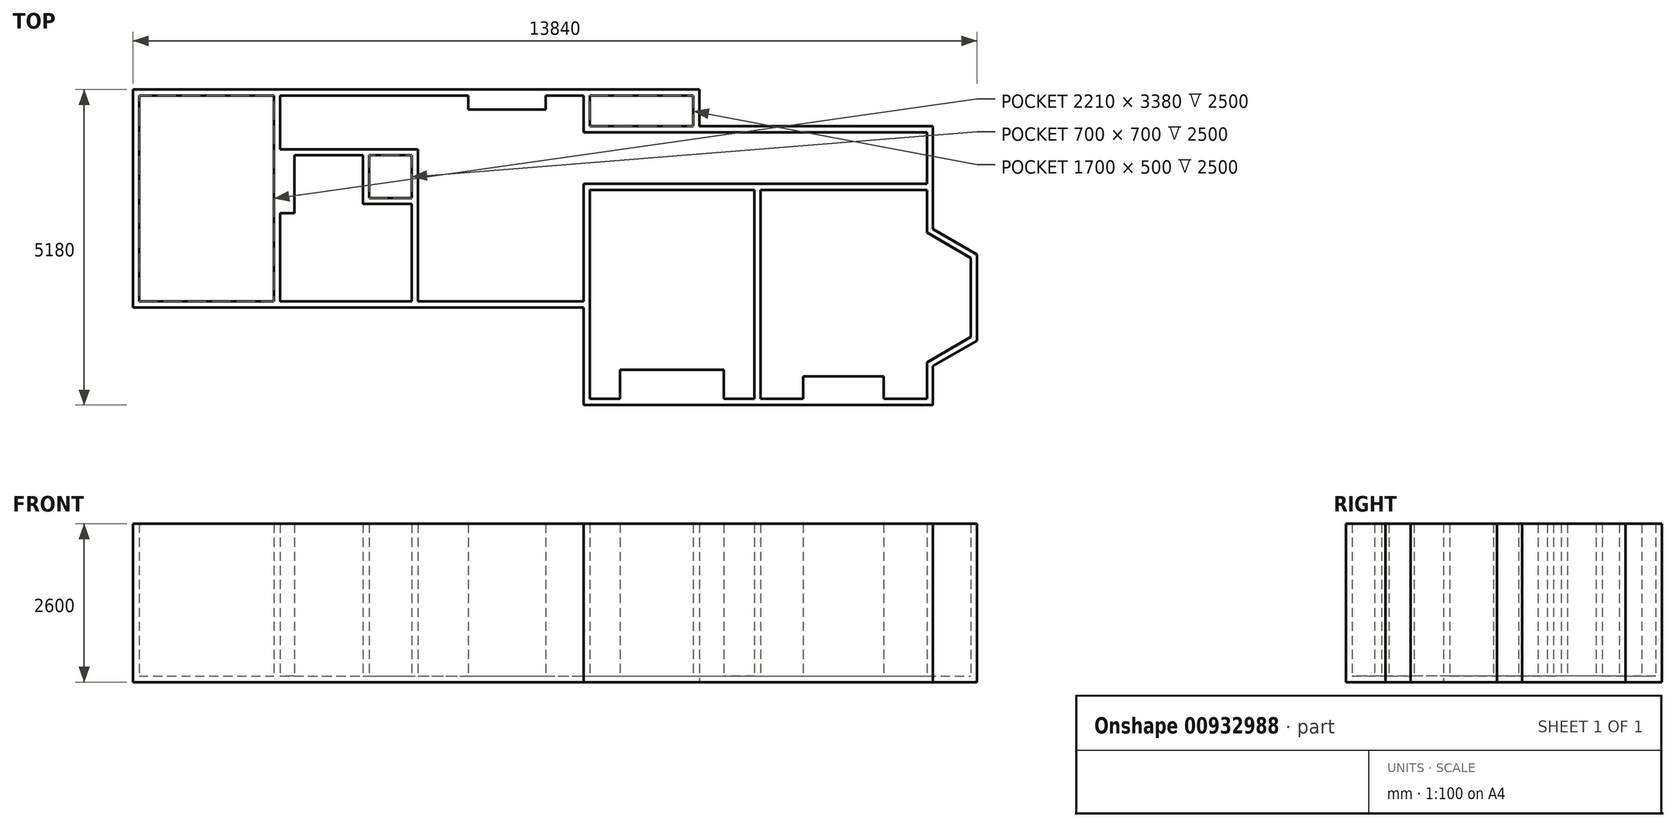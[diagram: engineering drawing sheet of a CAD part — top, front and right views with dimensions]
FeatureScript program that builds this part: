
annotation { "Feature Type Name" : "Feature", "Feature Type Description" : "" }
export const myFeature = defineFeature(function(context is Context, id is Id, definition is map)
    precondition{}
    {
        {
            var Q0;
            Q0=qCreatedBy(makeId("Top.planeOp"),FACE);
            var sketch = newSketch(context, id + "F0", { "sketchPlane" : qUnion([Q0])});
            skLineSegment(sketch, "E0", {"start": v(0, 0) * mm, "end": v(2210, 0) * mm});
            skLineSegment(sketch, "E1", {"start": v(0, 0) * mm, "end": v(0, -3380) * mm});
            skLineSegment(sketch, "E2", {"start": v(0, -3380) * mm, "end": v(2210, -3380) * mm});
            skLineSegment(sketch, "E3", {"start": v(7290, -600) * mm, "end": v(7290, 0) * mm});
            skLineSegment(sketch, "E4.0", {"start": v(-100, 100) * mm, "end": v(7390, 100) * mm});
            skLineSegment(sketch, "E4.1", {"start": v(-100, 100) * mm, "end": v(-100, -3480) * mm});
            skLineSegment(sketch, "E4.2", {"start": v(-100, -3480) * mm, "end": v(7290, -3480) * mm});
            skLineSegment(sketch, "E4.3", {"start": v(7390, -500) * mm, "end": v(7390, 0) * mm});
            skLineSegment(sketch, "E5", {"start": v(7290, 0) * mm, "end": v(7290, -600) * mm, "construction": true});
            skLineSegment(sketch, "E6", {"start": v(7390, -600) * mm, "end": v(11290, -600) * mm, "construction": true});
            skLineSegment(sketch, "E7", {"start": v(2210, -3380) * mm, "end": v(2210, 0) * mm});
            skLineSegment(sketch, "E8", {"start": v(2310, -3380) * mm, "end": v(2310, -1930) * mm});
            skLineSegment(sketch, "E9.trimOffspring", {"start": v(2310, 0) * mm, "end": v(5400, 0) * mm});
            skLineSegment(sketch, "E10.trimOffspring", {"start": v(2310, -3380) * mm, "end": v(4470, -3380) * mm});
            skLineSegment(sketch, "E11", {"start": v(2550, -980) * mm, "end": v(3670, -980) * mm});
            skLineSegment(sketch, "E12", {"start": v(4470, -1780) * mm, "end": v(4470, -3380) * mm});
            skLineSegment(sketch, "E13.0", {"start": v(4570, -880) * mm, "end": v(4570, -3380) * mm});
            skLineSegment(sketch, "E13.1", {"start": v(2310, -880) * mm, "end": v(4570, -880) * mm});
            skLineSegment(sketch, "E14.trimOffspring", {"start": v(2310, -880) * mm, "end": v(2310, 0) * mm});
            skLineSegment(sketch, "E15.trimOffspring", {"start": v(4570, -3380) * mm, "end": v(7290, -3380) * mm});
            skLineSegment(sketch, "E16", {"start": v(4570, 0) * mm, "end": v(5400, 0) * mm, "construction": true});
            skLineSegment(sketch, "E17", {"start": v(7290, 0) * mm, "end": v(6670, 0) * mm, "construction": true});
            skLineSegment(sketch, "E18", {"start": v(5400, 0) * mm, "end": v(5400, -230) * mm});
            skLineSegment(sketch, "E19", {"start": v(6670, -230) * mm, "end": v(6670, 0) * mm});
            skLineSegment(sketch, "E20", {"start": v(5400, -230) * mm, "end": v(6670, -230) * mm});
            skLineSegment(sketch, "E21.trimOffspring", {"start": v(6670, 0) * mm, "end": v(7290, 0) * mm});
            skLineSegment(sketch, "E22", {"start": v(3670, -980) * mm, "end": v(3670, -1780) * mm, "construction": true});
            skLineSegment(sketch, "E23", {"start": v(3670, -1780) * mm, "end": v(4470, -1780) * mm, "construction": true});
            skLineSegment(sketch, "E24.top", {"start": v(3670, -1780) * mm, "end": v(4470, -1780) * mm});
            skLineSegment(sketch, "E24.left", {"start": v(3670, -980) * mm, "end": v(3670, -1780) * mm});
            skLineSegment(sketch, "E25", {"start": v(2310, -3380) * mm, "end": v(2310, -1930) * mm, "construction": true});
            skLineSegment(sketch, "E26", {"start": v(3670, -980) * mm, "end": v(2550, -980) * mm});
            skLineSegment(sketch, "E27", {"start": v(2550, -980) * mm, "end": v(2550, -1930) * mm});
            skLineSegment(sketch, "E28", {"start": v(2550, -1930) * mm, "end": v(2310, -1930) * mm});
            skLineSegment(sketch, "E29", {"start": v(7390, -3480) * mm, "end": v(7390, -1550) * mm});
            skLineSegment(sketch, "E30", {"start": v(7390, -1450) * mm, "end": v(12620, -1450) * mm});
            skLineSegment(sketch, "E31", {"start": v(7390, -600) * mm, "end": v(12620, -600) * mm});
            skLineSegment(sketch, "E32.0", {"start": v(7390, -1550) * mm, "end": v(10090, -1550) * mm});
            skLineSegment(sketch, "E32.2", {"start": v(7390, -500) * mm, "end": v(9090, -500) * mm});
            skLineSegment(sketch, "E33", {"start": v(7390, -1550) * mm, "end": v(7390, -4980) * mm, "construction": true});
            skLineSegment(sketch, "E34.left", {"start": v(7390, -1550) * mm, "end": v(7390, -4980) * mm});
            skLineSegment(sketch, "E34.right", {"start": v(10090, -1550) * mm, "end": v(10090, -4980) * mm});
            skLineSegment(sketch, "E35.0", {"start": v(7290, -1550) * mm, "end": v(7290, -3380) * mm});
            skLineSegment(sketch, "E35.1", {"start": v(7290, -5080) * mm, "end": v(10190, -5080) * mm});
            skLineSegment(sketch, "E35.2", {"start": v(10190, -1550) * mm, "end": v(10190, -4980) * mm});
            skLineSegment(sketch, "E36.trimOffspring", {"start": v(7290, -3480) * mm, "end": v(7290, -5080) * mm});
            skLineSegment(sketch, "E37.trimOffspring", {"start": v(10190, -1550) * mm, "end": v(12720, -1550) * mm});
            skLineSegment(sketch, "E38", {"start": v(7390, -1450) * mm, "end": v(7290, -1450) * mm});
            skLineSegment(sketch, "E39", {"start": v(7290, -1450) * mm, "end": v(7290, -1550) * mm});
            skLineSegment(sketch, "E40", {"start": v(10190, -1550) * mm, "end": v(12920, -1550) * mm, "construction": true});
            skPoint(sketch, "E40.endSnap0", {"position": v(11455, -1550) * mm});
            skLineSegment(sketch, "E41.bottom", {"start": v(10190, -1550) * mm, "end": v(12920, -1550) * mm});
            skLineSegment(sketch, "E41.right", {"start": v(13640, -2665.7) * mm, "end": v(13640, -3964.3) * mm});
            skLineSegment(sketch, "E42.0", {"start": v(10190, -1450) * mm, "end": v(12920, -1450) * mm});
            skLineSegment(sketch, "E42.2", {"start": v(10190, -5080) * mm, "end": v(13020, -5080) * mm});
            skLineSegment(sketch, "E43", {"start": v(12920, -4980) * mm, "end": v(12920, -4380) * mm, "construction": true});
            skLineSegment(sketch, "E44", {"start": v(12920, -1550) * mm, "end": v(12920, -2250) * mm, "construction": true});
            skLineSegment(sketch, "E45", {"start": v(12920, -4980) * mm, "end": v(12920, -4380) * mm});
            skLineSegment(sketch, "E46", {"start": v(12920, -2250) * mm, "end": v(12920, -1550) * mm});
            skLineSegment(sketch, "E47", {"start": v(12920, -4980) * mm, "end": v(12210, -4980) * mm, "construction": true});
            skLineSegment(sketch, "E48.top", {"start": v(10890, -4610) * mm, "end": v(12210, -4610) * mm});
            skLineSegment(sketch, "E48.left", {"start": v(10890, -4980) * mm, "end": v(10890, -4610) * mm});
            skLineSegment(sketch, "E48.right", {"start": v(12210, -4980) * mm, "end": v(12210, -4610) * mm});
            skLineSegment(sketch, "E49.trimOffspring", {"start": v(12210, -4980) * mm, "end": v(12920, -4980) * mm});
            skLineSegment(sketch, "E50", {"start": v(12920, -2250) * mm, "end": v(13640, -2665.7) * mm});
            skLineSegment(sketch, "E51", {"start": v(12920, -4380) * mm, "end": v(13640, -3964.3) * mm});
            skPoint(sketch, "E52.start.orphan", {"position": v(13640, -4380) * mm});
            skPoint(sketch, "E53.orphan", {"position": v(13640, -1550) * mm});
            skLineSegment(sketch, "E54.0", {"start": v(13020, -2192.26) * mm, "end": v(13020, -1550) * mm});
            skLineSegment(sketch, "E54.1", {"start": v(13020, -4980) * mm, "end": v(13020, -4437.74) * mm});
            skLineSegment(sketch, "E54.2", {"start": v(13020, -4437.74) * mm, "end": v(13740, -4022.04) * mm});
            skLineSegment(sketch, "E54.3", {"start": v(13740, -2607.96) * mm, "end": v(13740, -4022.04) * mm});
            skLineSegment(sketch, "E54.4", {"start": v(13020, -2192.26) * mm, "end": v(13740, -2607.96) * mm});
            skLineSegment(sketch, "E55", {"start": v(12720, -500) * mm, "end": v(13020, -500) * mm});
            skLineSegment(sketch, "E56", {"start": v(13020, -500) * mm, "end": v(13020, -1550) * mm});
            skLineSegment(sketch, "E57", {"start": v(12620, -600) * mm, "end": v(12920, -600) * mm});
            skLineSegment(sketch, "E58", {"start": v(12920, -600) * mm, "end": v(12920, -1450) * mm});
            skLineSegment(sketch, "E59", {"start": v(13020, -4980) * mm, "end": v(13020, -5080) * mm});
            skLineSegment(sketch, "E60.trimOffspring", {"start": v(12210, -4980) * mm, "end": v(12920, -4980) * mm, "construction": true});
            skLineSegment(sketch, "E61", {"start": v(7290, -600) * mm, "end": v(7390, -600) * mm});
            skLineSegment(sketch, "E62", {"start": v(10190, -4980) * mm, "end": v(10890, -4980) * mm});
            skLineSegment(sketch, "E63.bottom", {"start": v(3770, -980) * mm, "end": v(4470, -980) * mm});
            skLineSegment(sketch, "E63.top", {"start": v(3770, -1680) * mm, "end": v(4470, -1680) * mm});
            skLineSegment(sketch, "E63.left", {"start": v(3770, -980) * mm, "end": v(3770, -1680) * mm});
            skLineSegment(sketch, "E63.right", {"start": v(4470, -980) * mm, "end": v(4470, -1680) * mm});
            skLineSegment(sketch, "E64", {"start": v(7390, -4980) * mm, "end": v(7890, -4980) * mm});
            skLineSegment(sketch, "E65", {"start": v(10090, -4980) * mm, "end": v(9590, -4980) * mm});
            skLineSegment(sketch, "E66", {"start": v(7890, -4500) * mm, "end": v(9590, -4500) * mm});
            skLineSegment(sketch, "E67", {"start": v(9590, -4500) * mm, "end": v(9590, -4980) * mm});
            skLineSegment(sketch, "E68", {"start": v(7890, -4500) * mm, "end": v(7890, -4980) * mm});
            skPoint(sketch, "E69.start.orphan", {"position": v(7890, -1550) * mm});
            skLineSegment(sketch, "E70.top", {"start": v(7390, 0) * mm, "end": v(9090, 0) * mm});
            skLineSegment(sketch, "E70.right", {"start": v(9090, -500) * mm, "end": v(9090, 0) * mm});
            skLineSegment(sketch, "E71", {"start": v(7390, 100) * mm, "end": v(9190, 100) * mm});
            skLineSegment(sketch, "E72", {"start": v(9190, 100) * mm, "end": v(9190, -500) * mm});
            skLineSegment(sketch, "E73.trimOffspring", {"start": v(9190, -500) * mm, "end": v(12720, -500) * mm});
            skSolve(sketch);
        }
        {
            var Q0;
            Q0 = qSketchRegion(id + "F0", true);
            extrude(context, id + "F1", {"entities" : qUnion([Q0]), "depth" : 2500 * mm, "offsetDistance" : 25 * mm});
        }
        {
            var Q0;
            Q0=makeQuery(id+"F1.opExtrude","CAP_FACE",FACE,{"disambiguationData":[OSD([sQuery(id+"F0.wireOp",EDGE,"E0"),sQuery(id+"F0.wireOp",EDGE,"E1"),sQuery(id+"F0.wireOp",EDGE,"E2"),sQuery(id+"F0.wireOp",EDGE,"E3"),sQuery(id+"F0.wireOp",EDGE,"E4.0"),sQuery(id+"F0.wireOp",EDGE,"E4.1"),sQuery(id+"F0.wireOp",EDGE,"E4.2"),sQuery(id+"F0.wireOp",EDGE,"E7"),sQuery(id+"F0.wireOp",EDGE,"E8"),sQuery(id+"F0.wireOp",EDGE,"E9.trimOffspring"),sQuery(id+"F0.wireOp",EDGE,"E10.trimOffspring"),sQuery(id+"F0.wireOp",EDGE,"E12"),sQuery(id+"F0.wireOp",EDGE,"E13.0"),sQuery(id+"F0.wireOp",EDGE,"E13.1"),sQuery(id+"F0.wireOp",EDGE,"E14.trimOffspring"),sQuery(id+"F0.wireOp",EDGE,"E15.trimOffspring"),sQuery(id+"F0.wireOp",EDGE,"E18"),sQuery(id+"F0.wireOp",EDGE,"E19"),sQuery(id+"F0.wireOp",EDGE,"E20"),sQuery(id+"F0.wireOp",EDGE,"E21.trimOffspring"),sQuery(id+"F0.wireOp",EDGE,"E24.top"),sQuery(id+"F0.wireOp",EDGE,"E24.left"),sQuery(id+"F0.wireOp",EDGE,"E26"),sQuery(id+"F0.wireOp",EDGE,"E27"),sQuery(id+"F0.wireOp",EDGE,"E28"),sQuery(id+"F0.wireOp",EDGE,"E30"),sQuery(id+"F0.wireOp",EDGE,"E31"),sQuery(id+"F0.wireOp",EDGE,"E32.0"),sQuery(id+"F0.wireOp",EDGE,"E34.left"),sQuery(id+"F0.wireOp",EDGE,"E34.right"),sQuery(id+"F0.wireOp",EDGE,"E35.0"),sQuery(id+"F0.wireOp",EDGE,"E35.1"),sQuery(id+"F0.wireOp",EDGE,"E36.trimOffspring"),sQuery(id+"F0.wireOp",EDGE,"E38"),sQuery(id+"F0.wireOp",EDGE,"E39"),sQuery(id+"F0.wireOp",EDGE,"E41.bottom"),sQuery(id+"F0.wireOp",EDGE,"E35.2"),sQuery(id+"F0.wireOp",EDGE,"E41.right"),sQuery(id+"F0.wireOp",EDGE,"E42.0"),sQuery(id+"F0.wireOp",EDGE,"E42.2"),sQuery(id+"F0.wireOp",EDGE,"E45"),sQuery(id+"F0.wireOp",EDGE,"E46"),sQuery(id+"F0.wireOp",EDGE,"E48.top"),sQuery(id+"F0.wireOp",EDGE,"E48.left"),sQuery(id+"F0.wireOp",EDGE,"E48.right"),sQuery(id+"F0.wireOp",EDGE,"E49.trimOffspring"),sQuery(id+"F0.wireOp",EDGE,"E50"),sQuery(id+"F0.wireOp",EDGE,"E51"),sQuery(id+"F0.wireOp",EDGE,"E54.0"),sQuery(id+"F0.wireOp",EDGE,"E54.1"),sQuery(id+"F0.wireOp",EDGE,"E54.2"),sQuery(id+"F0.wireOp",EDGE,"E54.3"),sQuery(id+"F0.wireOp",EDGE,"E54.4"),sQuery(id+"F0.wireOp",EDGE,"E55"),sQuery(id+"F0.wireOp",EDGE,"E56"),sQuery(id+"F0.wireOp",EDGE,"E57"),sQuery(id+"F0.wireOp",EDGE,"E58"),sQuery(id+"F0.wireOp",EDGE,"E59"),sQuery(id+"F0.wireOp",EDGE,"E61"),sQuery(id+"F0.wireOp",EDGE,"E62"),sQuery(id+"F0.wireOp",EDGE,"E63.bottom"),sQuery(id+"F0.wireOp",EDGE,"E63.top"),sQuery(id+"F0.wireOp",EDGE,"E63.left"),sQuery(id+"F0.wireOp",EDGE,"E63.right"),sQuery(id+"F0.wireOp",EDGE,"E64"),sQuery(id+"F0.wireOp",EDGE,"E65"),sQuery(id+"F0.wireOp",EDGE,"E66"),sQuery(id+"F0.wireOp",EDGE,"E67"),sQuery(id+"F0.wireOp",EDGE,"E68"),sQuery(id+"F0.wireOp",EDGE,"E32.2"),sQuery(id+"F0.wireOp",EDGE,"E70.top"),sQuery(id+"F0.wireOp",EDGE,"E4.3"),sQuery(id+"F0.wireOp",EDGE,"E70.right"),sQuery(id+"F0.wireOp",EDGE,"E71"),sQuery(id+"F0.wireOp",EDGE,"E72"),sQuery(id+"F0.wireOp",EDGE,"E73.trimOffspring")])],"isStart":true});
            var sketch = newSketch(context, id + "F2", { "sketchPlane" : qUnion([Q0])});
            skLineSegment(sketch, "E74.0", {"start": v(-100, 3480) * mm, "end": v(7290, 3480) * mm});
            skLineSegment(sketch, "E74.1", {"start": v(-100, -100) * mm, "end": v(9190, -100) * mm});
            skLineSegment(sketch, "E74.2", {"start": v(7290, 5080) * mm, "end": v(13020, 5080) * mm});
            skLineSegment(sketch, "E75.0", {"start": v(7290, 3480) * mm, "end": v(7290, 5080) * mm});
            skLineSegment(sketch, "E75.1", {"start": v(9190, -100) * mm, "end": v(9190, 500) * mm});
            skLineSegment(sketch, "E76.0", {"start": v(9190, 500) * mm, "end": v(13020, 500) * mm});
            skLineSegment(sketch, "E77.0", {"start": v(13020, 2192.26) * mm, "end": v(13020, 500) * mm});
            skLineSegment(sketch, "E78.0", {"start": v(13020, 2192.26) * mm, "end": v(13740, 2607.96) * mm});
            skLineSegment(sketch, "E79.0", {"start": v(13740, 2607.96) * mm, "end": v(13740, 4022.04) * mm});
            skLineSegment(sketch, "E80.0", {"start": v(13020, 4437.74) * mm, "end": v(13740, 4022.04) * mm});
            skLineSegment(sketch, "E81.0", {"start": v(13020, 4437.74) * mm, "end": v(13020, 5080) * mm});
            skLineSegment(sketch, "E82", {"start": v(13740, 2607.96) * mm, "end": v(13020, 2192.26) * mm});
            skLineSegment(sketch, "E83", {"start": v(13020, 500) * mm, "end": v(9190, 500) * mm});
            skLineSegment(sketch, "E84", {"start": v(9190, -100) * mm, "end": v(-100, -100) * mm});
            skLineSegment(sketch, "E85", {"start": v(-100, 3480) * mm, "end": v(-100, -100) * mm});
            skSolve(sketch);
        }
        {
            var Q0;
            Q0 = qSketchRegion(id + "F2", true);
            extrude(context, id + "F3", {"entities" : qUnion([Q0]), "operationType" : NewBodyOperationType.ADD, "depth" : 100 * mm, "offsetDistance" : 25 * mm});
        }
    });
